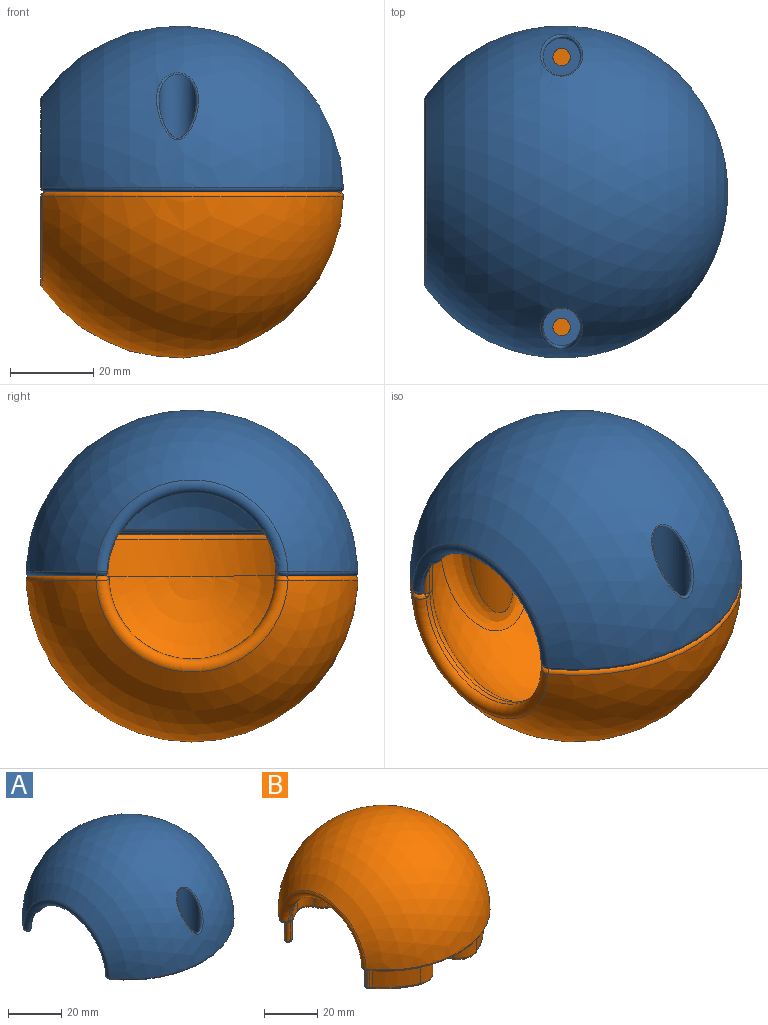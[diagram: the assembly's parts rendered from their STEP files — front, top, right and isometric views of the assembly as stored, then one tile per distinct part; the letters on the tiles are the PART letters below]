
ASSEMBLY  parts=2 mates=1
PART A: 92 faces, bbox 78.6x86.6x50.3 mm
  f0: sphere r=35mm, area 4186.1mm2, adj f5,f6,f7,f59,f63,f67
  f1: plane 77.97x70.97mm, normal (0,0,-1), area 345.5mm2, adj f9,f10,f34,f35,f36,f39,f40,f41
  f2: cylinder r=20mm len=33.47mm, axis (1,0,0), area 49mm2, adj f7,f17,f57,f69
  f3: cylinder r=8mm len=13.45mm, axis (0,0,-1), area 126mm2, adj f6,f61
  f4: cylinder r=8mm len=13.45mm, axis (0,0,-1), area 126mm2, adj f5,f65
  f5: bspline ~27.12x19.59mm, area 215.9mm2, adj f0,f4,f64,f66
  f6: bspline ~27.04x19.7mm, area 215.9mm2, adj f0,f3,f60,f62
  f7: torus R=22mm, axis (1,0,0), area 75.6mm2, adj f0,f2,f58,f68
  f8: sphere r=40mm, area 8608.4mm2, adj f15,f16,f17,f35
  f9: cylinder r=2.1mm len=5mm, axis (0,0,-1), area 66mm2, adj f1,f13
  f10: cylinder r=2.1mm len=5mm, axis (0,0,-1), area 66mm2, adj f1,f12
  f11: cylinder r=4.5mm len=23.36mm, axis (0,0,-1), area 439.7mm2, adj f12,f15
  f12: plane 9x9mm, normal (0,0,1), area 49.8mm2, adj f10,f11
  f13: plane 9x9mm, normal (0,0,1), area 49.8mm2, adj f9,f14
  f14: cylinder r=4.5mm len=23.36mm, axis (0,0,-1), area 457.9mm2, adj f13,f16
  f15: bspline ~16.31x10.13mm, area 39.8mm2, adj f8,f11
  f16: bspline ~16.31x10.14mm, area 39.9mm2, adj f8,f14
  f17: torus R=22mm, axis (1,0,0), area 252.5mm2, adj f2,f8,f34,f36,f37,f55,f56,f70
  f18: plane 8.6x2.77mm, normal (1,0,0), area 11.6mm2, adj f33,f37,f38,f39,f74
  f19: plane 67.99x66.79mm, normal (0,0,-1), area 377.1mm2, adj f57,f58,f59,f60,f61,f62,f63,f64
  f20: plane 8.6x2.77mm, normal (1,0,0), area 11.6mm2, adj f32,f53,f54,f55,f88
  f21: cylinder r=37.6mm len=14.3mm, axis (0,0,-1), area 156.4mm2, adj f22,f30,f50,f85
  f22: cylinder r=7.6mm len=10.05mm, axis (0,0,-1), area 103.7mm2, adj f21,f23,f49,f84
  f23: cylinder r=5.4mm len=9.97mm, axis (0,0,-1), area 109.2mm2, adj f22,f24,f48,f83
  f24: cylinder r=7.6mm len=10.05mm, axis (0,0,-1), area 103.7mm2, adj f23,f25,f47,f82
  f25: cylinder r=37.6mm len=68.92mm, axis (0,0,-1), area 749.8mm2, adj f24,f26,f46,f81
  f26: cylinder r=7.6mm len=10.05mm, axis (0,0,-1), area 103.7mm2, adj f25,f27,f45,f80
  f27: cylinder r=5.4mm len=9.97mm, axis (0,0,-1), area 109.2mm2, adj f26,f28,f44,f79
  f28: cylinder r=7.6mm len=10.05mm, axis (0,0,-1), area 103.7mm2, adj f27,f29,f43,f78
  f29: cylinder r=37.6mm len=14.3mm, axis (0,0,-1), area 156.4mm2, adj f28,f31,f42,f77
  f30: cylinder r=2.5mm len=8.6mm, axis (0,0,-1), area 10.1mm2, adj f21,f32,f51,f86
  f31: cylinder r=2.5mm len=8.6mm, axis (0,0,-1), area 10.1mm2, adj f29,f33,f41,f76
  f32: cylinder r=1.25mm len=8.6mm, axis (0,0,-1), area 12.3mm2, adj f20,f30,f52,f87
  f33: cylinder r=1.25mm len=8.6mm, axis (0,0,-1), area 12.3mm2, adj f18,f31,f40,f75
  f34: bspline ~3.03x1.43mm, area 3.5mm2, adj f1,f17,f35,f38
  f35: torus R=38.99mm, axis (0,0,-1), area 319.4mm2, adj f1,f8,f34,f36
  f36: bspline ~3.03x1.43mm, area 3.5mm2, adj f1,f17,f35,f54
  f37: torus R=21.11mm, axis (-1,0,0), area 17.7mm2, adj f17,f18,f38,f71,f72,f73
  f38: bspline ~2.43x1.35mm, area 2.1mm2, adj f18,f34,f37,f39
  f39: cylinder r=0.8mm len=0.8mm, axis (0,-1,0), area 0.4mm2, adj f1,f18,f38,f40
  f40: torus R=2.05mm, axis (0,0,-1), area 2.2mm2, adj f1,f33,f39,f41
  f41: torus R=1.7mm, axis (0,0,-1), area 1.3mm2, adj f1,f31,f40,f42
  f42: torus R=38.4mm, axis (0,0,-1), area 23mm2, adj f1,f29,f41,f43
  f43: torus R=8.4mm, axis (0,0,-1), area 15.7mm2, adj f1,f28,f42,f44
  f44: torus R=4.6mm, axis (0,0,-1), area 15.1mm2, adj f1,f27,f43,f45
  f45: torus R=8.4mm, axis (0,0,-1), area 15.7mm2, adj f1,f26,f44,f46
  f46: torus R=38.4mm, axis (0,0,-1), area 110.4mm2, adj f1,f25,f45,f47
  f47: torus R=8.4mm, axis (0,0,-1), area 15.7mm2, adj f1,f24,f46,f48
  f48: torus R=4.6mm, axis (0,0,-1), area 15.1mm2, adj f1,f23,f47,f49
  f49: torus R=8.4mm, axis (0,0,-1), area 15.7mm2, adj f1,f22,f48,f50
  f50: torus R=38.4mm, axis (0,0,-1), area 23mm2, adj f1,f21,f49,f51
  f51: torus R=1.7mm, axis (0,0,-1), area 1.3mm2, adj f1,f30,f50,f52
  f52: torus R=2.05mm, axis (0,0,-1), area 2.2mm2, adj f1,f32,f51,f53
  f53: cylinder r=0.8mm len=0.8mm, axis (0,-1,0), area 0.4mm2, adj f1,f20,f52,f54
  f54: bspline ~2.43x1.67mm, area 2.1mm2, adj f20,f36,f53,f55
  f55: torus R=21.11mm, axis (-1,0,0), area 17.7mm2, adj f17,f20,f54,f89,f90,f91
  f56: bspline ~1.89x1.26mm, area 0.4mm2, adj f17,f57,f71
  f57: cylinder r=1mm len=1.24mm, axis (1,0,0), area 1.1mm2, adj f2,f19,f56,f58,f72
  f58: bspline ~2.29x1.63mm, area 1.6mm2, adj f7,f19,f57,f59
  f59: torus R=34.11mm, axis (0,0,-1), area 25.3mm2, adj f0,f19,f58,f60
  f60: bspline ~9.53x4.91mm, area 10.9mm2, adj f6,f19,f59,f61
  f61: torus R=7mm, axis (0,0,-1), area 24mm2, adj f3,f19,f60,f62
  f62: bspline ~8.71x4.91mm, area 10.9mm2, adj f6,f19,f61,f63
  f63: torus R=34.11mm, axis (0,0,-1), area 97.2mm2, adj f0,f19,f62,f64
  f64: bspline ~9.53x4.91mm, area 10.9mm2, adj f5,f19,f63,f65
  f65: torus R=7mm, axis (0,0,-1), area 24mm2, adj f4,f19,f64,f66
  f66: bspline ~8.71x4.91mm, area 10.9mm2, adj f5,f19,f65,f67
  f67: torus R=34.11mm, axis (0,0,-1), area 25.3mm2, adj f0,f19,f66,f68
  f68: bspline ~2.29x1.63mm, area 1.6mm2, adj f7,f19,f67,f69
  f69: cylinder r=1mm len=1.24mm, axis (1,0,0), area 1.1mm2, adj f2,f19,f68,f70,f90
  f70: bspline ~1.89x1.26mm, area 0.4mm2, adj f17,f69,f91
  f71: bspline ~1.43x1.14mm, area 0.4mm2, adj f37,f56,f72
  f72: bspline ~1.37x1.12mm, area 0.7mm2, adj f37,f57,f71,f73
  f73: bspline ~2.17x1.39mm, area 1.6mm2, adj f19,f37,f72,f74
  f74: cylinder r=1.1mm len=2.77mm, axis (0,1,0), area 4.8mm2, adj f18,f19,f73,f75
  f75: torus R=0.15mm, axis (0,0,-1), area 1.7mm2, adj f19,f33,f74,f76
  f76: torus R=3.6mm, axis (0,0,-1), area 2.3mm2, adj f19,f31,f75,f77
  f77: torus R=36.5mm, axis (0,0,-1), area 31.1mm2, adj f19,f29,f76,f78
  f78: torus R=6.5mm, axis (0,0,-1), area 19.7mm2, adj f19,f28,f77,f79
  f79: torus R=6.5mm, axis (0,0,-1), area 23.6mm2, adj f19,f27,f78,f80
  f80: torus R=6.5mm, axis (0,0,-1), area 19.7mm2, adj f19,f26,f79,f81
  f81: torus R=36.5mm, axis (0,0,-1), area 149mm2, adj f19,f25,f80,f82
  f82: torus R=6.5mm, axis (0,0,-1), area 19.7mm2, adj f19,f24,f81,f83
  f83: torus R=6.5mm, axis (0,0,-1), area 23.6mm2, adj f19,f23,f82,f84
  f84: torus R=6.5mm, axis (0,0,-1), area 19.7mm2, adj f19,f22,f83,f85
  f85: torus R=36.5mm, axis (0,0,-1), area 31.1mm2, adj f19,f21,f84,f86
  f86: torus R=3.6mm, axis (0,0,-1), area 2.3mm2, adj f19,f30,f85,f87
  f87: torus R=0.15mm, axis (0,0,-1), area 1.7mm2, adj f19,f32,f86,f88
  f88: cylinder r=1.1mm len=2.77mm, axis (0,1,0), area 4.8mm2, adj f19,f20,f87,f89
  f89: bspline ~2.17x1.39mm, area 1.6mm2, adj f19,f55,f88,f90
  f90: bspline ~1.37x1.12mm, area 0.7mm2, adj f55,f69,f89,f91
  f91: bspline ~1.43x1.14mm, area 0.4mm2, adj f55,f70,f90
PART B: 68 faces, bbox 78.6x86.6x50.3 mm
  f0: plane 1.43x1.39mm, normal (0,0,-1), area 0.3mm2, adj f54,f56,f59,f60
  f1: sphere r=35mm, area 5551.7mm2, adj f11,f12,f14,f17,f20,f23
  f2: sphere r=40mm, area 8909.4mm2, adj f13,f64
  f3: plane 77.97x70.97mm, normal (0,0,-1), area 530.5mm2, adj f7,f9,f15,f25,f26,f27,f28,f29
  f4: cylinder r=20mm len=40mm, axis (1,0,0), area 75.9mm2, adj f13,f14,f61,f62,f66,f67
  f5: cylinder r=8mm len=31.55mm, axis (0,0,-1), area 496.2mm2, adj f12,f18,f19,f49
  f6: cylinder r=8mm len=31.55mm, axis (0,0,-1), area 496.3mm2, adj f11,f21,f22,f55
  f7: cylinder r=2.1mm len=15mm, axis (0,0,-1), area 197.9mm2, adj f3,f8
  f8: plane 4.2x4.2mm, normal (0,0,-1), area 13.9mm2, adj f7
  f9: cylinder r=2.1mm len=15mm, axis (0,0,-1), area 197.9mm2, adj f3,f10
  f10: plane 4.2x4.2mm, normal (0,0,-1), area 13.9mm2, adj f9
  f11: bspline ~29.99x28.01mm, area 397mm2, adj f1,f6,f21,f22
  f12: bspline ~28.87x28.01mm, area 397.1mm2, adj f1,f5,f18,f19
  f13: torus R=22mm, axis (1,0,0), area 283.7mm2, adj f2,f4,f63,f65
  f14: torus R=22mm, axis (1,0,0), area 119mm2, adj f1,f4,f16,f24,f61,f66
  f15: plane 8.75x0.3mm, normal (-1,0,0), area 2.6mm2, adj f3,f38,f39,f42
  f16: cylinder r=2mm len=8.75mm, axis (0,0,1), area 16mm2, adj f14,f17,f39,f46
  f17: cylinder r=35mm len=14.14mm, axis (0,0,1), area 160mm2, adj f1,f16,f18,f47
  f18: cylinder r=5mm len=8.75mm, axis (0,0,1), area 69.4mm2, adj f5,f12,f17,f48
  f19: cylinder r=5mm len=8.75mm, axis (0,0,1), area 69.4mm2, adj f5,f12,f20,f50
  f20: cylinder r=35mm len=64.16mm, axis (0,0,1), area 710.1mm2, adj f1,f19,f21,f51
  f21: cylinder r=5mm len=8.75mm, axis (0,0,1), area 69.4mm2, adj f6,f11,f20,f52
  f22: cylinder r=5mm len=8.75mm, axis (0,0,1), area 69.4mm2, adj f6,f11,f23,f58
  f23: cylinder r=35mm len=14.14mm, axis (0,0,1), area 160mm2, adj f1,f22,f24,f59
  f24: cylinder r=2mm len=8.75mm, axis (0,0,1), area 16mm2, adj f14,f23,f40,f60
  f25: plane 8.75x0.3mm, normal (-1,0,0), area 2.6mm2, adj f3,f40,f41,f54
  f26: cylinder r=37.5mm len=14.29mm, axis (0,0,1), area 159mm2, adj f3,f27,f36,f59
  f27: cylinder r=7.5mm len=9.92mm, axis (0,0,1), area 104.2mm2, adj f3,f26,f28,f58
  f28: cylinder r=5.5mm len=10.15mm, axis (0,0,1), area 113.2mm2, adj f3,f27,f29,f55
  f29: cylinder r=7.5mm len=9.92mm, axis (0,0,1), area 104.2mm2, adj f3,f28,f30,f52
  f30: cylinder r=37.5mm len=68.74mm, axis (0,0,1), area 760.8mm2, adj f3,f29,f31,f51
  f31: cylinder r=7.5mm len=9.92mm, axis (0,0,1), area 104.2mm2, adj f3,f30,f32,f50
  f32: cylinder r=5.5mm len=10.15mm, axis (0,0,1), area 113.2mm2, adj f3,f31,f33,f49
  f33: cylinder r=7.5mm len=9.92mm, axis (0,0,1), area 104.2mm2, adj f3,f32,f34,f48
  f34: cylinder r=37.5mm len=14.29mm, axis (0,0,1), area 159mm2, adj f3,f33,f37,f47
  f35: plane 1.43x1.39mm, normal (0,0,-1), area 0.3mm2, adj f42,f45,f46,f47
  f36: cylinder r=2.5mm len=8.75mm, axis (0,0,-1), area 10.6mm2, adj f3,f26,f41,f56
  f37: cylinder r=2.5mm len=8.75mm, axis (0,0,-1), area 10.6mm2, adj f3,f34,f38,f45
  f38: cylinder r=1.25mm len=8.75mm, axis (0,0,-1), area 12.7mm2, adj f3,f15,f37,f43
  f39: cylinder r=1.25mm len=8.75mm, axis (0,0,1), area 17.4mm2, adj f3,f15,f16,f44,f61
  f40: cylinder r=1.25mm len=8.75mm, axis (0,0,1), area 17.4mm2, adj f3,f24,f25,f57,f66
  f41: cylinder r=1.25mm len=8.75mm, axis (0,0,-1), area 12.7mm2, adj f3,f25,f36,f53
  f42: cylinder r=1.25mm len=1.25mm, axis (0,-1,0), area 0.6mm2, adj f15,f35,f43,f44
  f43: sphere r=1.25mm, area 1.8mm2, adj f38,f42,f45
  f44: sphere r=1.25mm, area 2.5mm2, adj f39,f42,f46
  f45: torus R=3.75mm, axis (0,0,-1), area 2.8mm2, adj f35,f37,f43,f47
  f46: torus R=0.75mm, axis (0,0,-1), area 2.8mm2, adj f16,f35,f44,f47
  f47: torus R=36.25mm, axis (0,0,-1), area 71.6mm2, adj f17,f34,f35,f45,f46,f48
  f48: torus R=6.25mm, axis (0,0,-1), area 39mm2, adj f18,f33,f47,f49
  f49: torus R=6.75mm, axis (0,0,-1), area 62.3mm2, adj f5,f32,f48,f50
  f50: torus R=6.25mm, axis (0,0,-1), area 39mm2, adj f19,f31,f49,f51
  f51: torus R=36.25mm, axis (0,0,-1), area 330.1mm2, adj f20,f30,f50,f52
  f52: torus R=6.25mm, axis (0,0,-1), area 39mm2, adj f21,f29,f51,f55
  f53: sphere r=1.25mm, area 1.8mm2, adj f41,f54,f56
  f54: cylinder r=1.25mm len=1.25mm, axis (0,-1,0), area 0.6mm2, adj f0,f25,f53,f57
  f55: torus R=6.75mm, axis (0,0,-1), area 62.3mm2, adj f6,f28,f52,f58
  f56: torus R=3.75mm, axis (0,0,-1), area 2.8mm2, adj f0,f36,f53,f59
  f57: sphere r=1.25mm, area 2.5mm2, adj f40,f54,f60
  f58: torus R=6.25mm, axis (0,0,-1), area 39mm2, adj f22,f27,f55,f59
  f59: torus R=36.25mm, axis (0,0,-1), area 71.6mm2, adj f0,f23,f26,f56,f58,f60
  f60: torus R=0.75mm, axis (0,0,-1), area 2.8mm2, adj f0,f24,f57,f59
  f61: bspline ~1.43x1.03mm, area 1mm2, adj f4,f14,f39,f62
  f62: cylinder r=1mm len=1mm, axis (1,0,0), area 0mm2, adj f3,f4,f61,f63
  f63: bspline ~3.52x2.45mm, area 5.5mm2, adj f3,f13,f62,f64
  f64: torus R=38.99mm, axis (0,0,-1), area 319.4mm2, adj f2,f3,f63,f65
  f65: bspline ~3.52x2.45mm, area 5.5mm2, adj f3,f13,f64,f67
  f66: bspline ~1.43x1.03mm, area 1mm2, adj f4,f14,f40,f67
  f67: cylinder r=1mm len=1mm, axis (1,0,0), area 0mm2, adj f3,f4,f65,f66
PLACE A at identity
PLACE B rot(axis=(1,0,0),180deg) t=(0,0,0)mm
MATE fastened B.f17 <-> A.f59  axis (0,0,-1) through (0,0,0)mm
